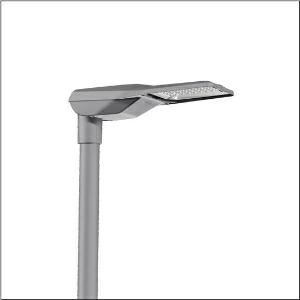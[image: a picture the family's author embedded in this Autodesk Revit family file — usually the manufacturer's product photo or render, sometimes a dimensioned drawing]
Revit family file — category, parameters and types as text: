
# Revit family: streetlight_sl_21_iq_mini___stw1_0a_5xe2e21d08hb_2a42
name_source: partatom
category: Lighting Fixtures
units: mm (PartAtom-declared; Revit-internal decimal feet)

## family parameters
Cut with Voids When Loaded = No
Host = Face
Light Source = No
Part Type = Normal
Room Calculation Point = No
Round Connector Dimension = Use Diameter
Shared = No

## types (1)
- --- (1 x LED, 7830 lm, 70.9 W, 2200K)
    Apparent Load = 71 VA
    CIE Flux Codes = 38 75 98 100 100
    Color Rendering = 70
    Color Temperature = 2200K
    Default Elevation = 1800 mm
    Description = Streetlight SL 21 iQ mini, mast luminaire, primary light control with lens, of PMMA, primary optical cover: cover, of toughened safety glass, transparent, light distribution: STW1.0a, light emission: direct distribution, primary light characteristic: asymmetric, installation type: post-top, side-entry, LED, High Power LED, rated luminous flux: 7.830lm, luminous efficacy: 110lm/W, light colour: 722, colour temperature: 2200K, control: Auto-Match, Temp-Guard, Lumen-Switch, Night-Set, Smart-Wire, Light-Fading, Desk-Remote (wireless, voltage-free reading and setting of iQ features in the workshop via application-optimized NFC function/RFID function), optimised constant luminous flux control (CLO 2.0), presetting dimming linear, mains connection: 220..240V, AC, 50/60Hz, start of lifetime: 71W, end of service life: 75W, reduction: 31W, luminaire housing, of diecast aluminium, powder-coated, Siteco® metallic grey (DB 702S), corrosivity category C5 mid according to DIN EN ISO 12944, please order mast flange separately, inclination adjustable: 0°, 5°, 10°, 15°, sealing non-destructively replaceable, multi-level sealing system, length: 628mm, width: 235mm, height: 110mm, mast flange for spigot size: 42mm (side-entry): 5XC10008XM4, 60/48mm (side-entry/post-top): 5XC10108XM2, 76/60mm (side-entry/post-top): 5XC10108XM1, protection rating (complete): IP66, insulation class (complete): insulation class II (safety insulation), certification: CE, ENEC, ENEC+, VDE, impact resistance: IK09, permissible operating ambient temperature for outdoor applications: -40..+50°C, standard-compliant lighting for roads and squares, packaging unit: 1 piece

Light Distribution: STW1.0a
    Height = 110 mm
    Lamp = 1 x LED
    Lamp Light Flux = 7830 lm
    Lamp Power = 70.9 W
    Lamp count = 1
    Length = 625 mm
    Luminous efficacy = 110 lm/W
    Manufacturer = Siteco
    ModVariant = No
    Model = 5XE2E21D08HB
    Number of Poles = 1
    OnlyDefault = Yes
    Power Factor = 1
    Product Name = Streetlight SL 21 iQ mini | STW1.0a
    Product group = mast luminaire | pylon top
    ProductGroupID = 6100
    Protection Class = Protection class II
    Protection Degree = IP 66
    RLX_Detail_Level = 1
    RLX_Emergency_Light_Flux = 0 lm
    RLX_Emergency_Type = 0
    RLX_Emergency_Type_DB = No
    RlxData = <blob elided: 91957 chars, md5=b79c4379>
    Socket = socket
    Standby Power = 0 W
    System Light Flux = 7830 lm
    System Power = 71 W
    Type Comments = factory setting: luminous flux: 100 % | dim-lin: 254 | 711 mA
    Type Image = l_1003519.jpg
    URL = http://relux.com
    VarID = @adj_108195
    Voltage = 0 V
    Weight = 0.00 kg
    Width = 234 mm

## geometry (parser evidence)
native form markers: Blend x4, Sweep x11
no freeform markers — native parametric forms only
